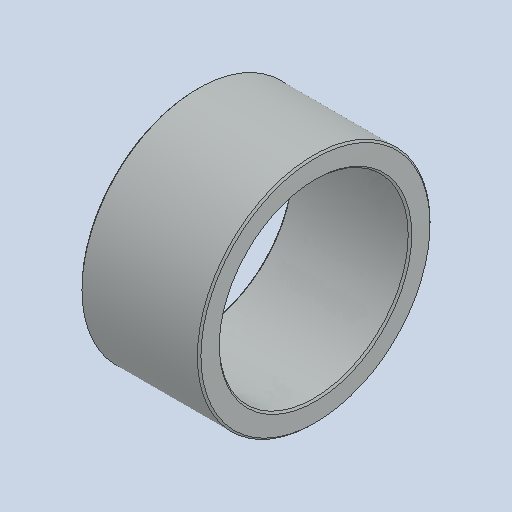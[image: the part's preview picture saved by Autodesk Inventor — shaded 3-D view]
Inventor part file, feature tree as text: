
AUTODESK INVENTOR PART (.ipt)
format: ipt  version: 2024.1 (Build 281209000, 209)  size: 116,736 bytes
history: native  units: in
note: dims shown in document units (in); Inventor stores cm internally (conversion verified against a paired STEP export)
features: chamfer x1
ambient origin geometry x8: Origin, YZ Plane, XZ Plane, XY Plane, X Axis, Y Axis, Z Axis, Center Point
bodies: Solid1 (feature_tree)
feature tree (1):
  chamfer  "Chamfer1"  [1 undecoded]
note: 1 required parameter value undecoded (feature->parameter linkage not recoverable at this tier; creation-order binding heuristic only, values carry confidence <= 0.55)
